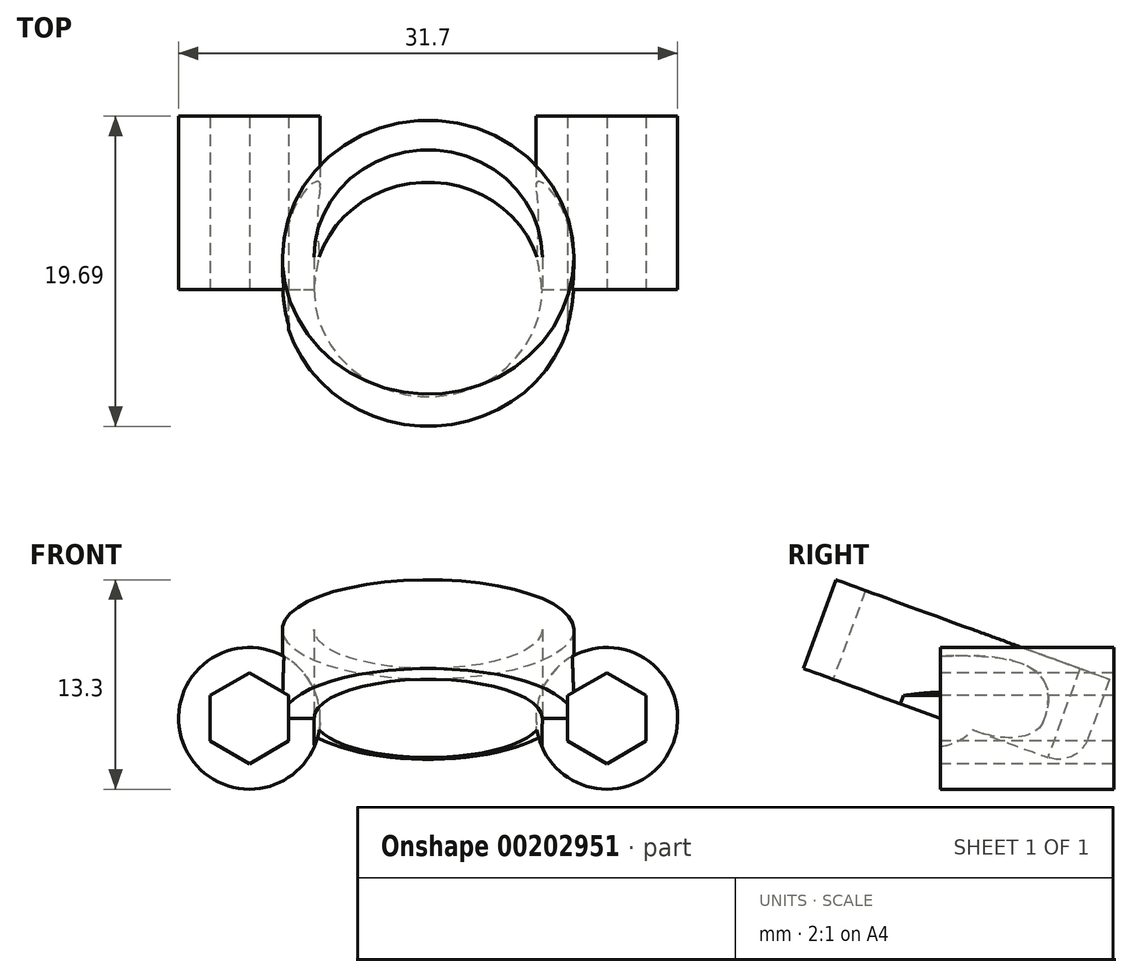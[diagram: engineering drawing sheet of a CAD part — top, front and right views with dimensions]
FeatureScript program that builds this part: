
annotation { "Feature Type Name" : "Feature", "Feature Type Description" : "" }
export const myFeature = defineFeature(function(context is Context, id is Id, definition is map)
    precondition{}
    {
        {
            var Q0;
            Q0=qCreatedBy(makeId("Top.planeOp"),FACE);
            var sketch = newSketch(context, id + "F0", { "sketchPlane" : qUnion([Q0])});
            skCircle(sketch, "E0", {"center": v(0, 0) * mm, "radius": 7.25 * mm});
            skCircle(sketch, "E1", {"center": v(0, 0) * mm, "radius": 9.25 * mm});
            skSolve(sketch);
        }
        {
            var Q0;
            Q0=makeQuery(id+"F0.imprint","IMPRINT",FACE,{"disambiguationData":[TD([[makeQuery(id+"F0.imprint","IMPRINT",EDGE,{"derivedFrom":sQuery(id+"F0.wireOp",EDGE,"E0")}),-1.0]])]});
            extrude(context, id + "F1", {"entities" : qUnion([Q0]), "depth" : 6 * mm});
        }
        {
            var Q0;
            Q0=qCreatedBy(makeId("Top.planeOp"),FACE);
            var sketch = newSketch(context, id + "F2", { "sketchPlane" : qUnion([Q0])});
            skLineSegment(sketch, "E2", {"start": v(-15.14, 0) * mm, "end": v(14.33, 0) * mm});
            skSolve(sketch);
        }
        {
            var Q0;
            Q0=makeQuery(id+"F1.opExtrude","SWEPT_BODY",BODY,{"disambiguationData":[OSD([sQuery(id+"F0.wireOp",EDGE,"E0"),sQuery(id+"F0.wireOp",EDGE,"h9PfKkJo-UdOM-yz0z-Uwii-sodwroVbnJnT.bottom"),sQuery(id+"F0.wireOp",EDGE,"h9PfKkJo-UdOM-yz0z-Uwii-sodwroVbnJnT.top"),sQuery(id+"F0.wireOp",EDGE,"h9PfKkJo-UdOM-yz0z-Uwii-sodwroVbnJnT.left"),sQuery(id+"F0.wireOp",EDGE,"h9PfKkJo-UdOM-yz0z-Uwii-sodwroVbnJnT.right")])]});
            var Q1;
            Q1=sQuery(id+"F2.wireOp",EDGE,"E2");
            var Q2;
            Q2=sQuery(id+"F2.wireOp",EDGE,"E2");
            transform(context, id + "F3", {"entities" : qUnion([Q0]), "transformType" : TransformType.ROTATION, "transformAxis" : qUnion([Q2]), "angle" : 20 * degree, "oppositeDirection" : true, "makeCopy" : false});
        }
        {
            var Q0;
            Q0=qCreatedBy(makeId("Front.planeOp"),FACE);
            var sketch = newSketch(context, id + "F4", { "sketchPlane" : qUnion([Q0])});
            skCircle(sketch, "E3.cCircle", {"center": v(-11.35, 0) * mm, "radius": 2.5 * mm, "construction": true});
            skLineSegment(sketch, "E3.0", {"start": v(-8.85, 1.44) * mm, "end": v(-8.85, -1.44) * mm});
            skLineSegment(sketch, "E3.1", {"start": v(-8.85, -1.44) * mm, "end": v(-11.35, -2.89) * mm});
            skLineSegment(sketch, "E3.2", {"start": v(-11.35, -2.89) * mm, "end": v(-13.85, -1.44) * mm});
            skLineSegment(sketch, "E3.3", {"start": v(-13.85, -1.44) * mm, "end": v(-13.85, 1.44) * mm});
            skLineSegment(sketch, "E3.4", {"start": v(-13.85, 1.44) * mm, "end": v(-11.35, 2.89) * mm});
            skLineSegment(sketch, "E3.5", {"start": v(-11.35, 2.89) * mm, "end": v(-8.85, 1.44) * mm});
            skPoint(sketch, "E3.0.midPoint", {"position": v(-8.85, 0) * mm});
            skCircle(sketch, "E4", {"center": v(-11.35, 0) * mm, "radius": 4.5 * mm});
            skCircle(sketch, "E5.1.0.0", {"center": v(11.35, 0) * mm, "radius": 4.5 * mm});
            skLineSegment(sketch, "E5.1.0.1", {"start": v(11.35, 2.89) * mm, "end": v(13.85, 1.44) * mm});
            skLineSegment(sketch, "E5.1.0.2", {"start": v(8.85, 1.44) * mm, "end": v(11.35, 2.89) * mm});
            skLineSegment(sketch, "E5.1.0.3", {"start": v(8.85, -1.44) * mm, "end": v(8.85, 1.44) * mm});
            skLineSegment(sketch, "E5.1.0.4", {"start": v(11.35, -2.89) * mm, "end": v(8.85, -1.44) * mm});
            skLineSegment(sketch, "E5.1.0.5", {"start": v(13.85, -1.44) * mm, "end": v(11.35, -2.89) * mm});
            skLineSegment(sketch, "E5.1.0.6", {"start": v(13.85, 1.44) * mm, "end": v(13.85, -1.44) * mm});
            skCircle(sketch, "E5.1.0.7", {"center": v(11.35, 0) * mm, "radius": 2.5 * mm, "construction": true});
            skPoint(sketch, "E5.1.0.8", {"position": v(13.85, 0) * mm});
            skLineSegment(sketch, "E5.direction1", {"start": v(-13.85, -1.44) * mm, "end": v(8.85, -1.44) * mm, "construction": true});
            skSolve(sketch);
        }
        {
            var Q0;
            Q0=makeQuery(id+"F4.imprint","IMPRINT",FACE,{"disambiguationData":[TD([[makeQuery(id+"F4.imprint","IMPRINT",EDGE,{"derivedFrom":sQuery(id+"F4.wireOp",EDGE,"E5.1.0.0")}),1.0]])]});
            var Q1;
            Q1=makeQuery(id+"F4.imprint","IMPRINT",FACE,{"disambiguationData":[TD([[makeQuery(id+"F4.imprint","IMPRINT",EDGE,{"derivedFrom":sQuery(id+"F4.wireOp",EDGE,"E3.0")}),1.0]])]});
            var Q2;
            Q2=makeQuery(id+"F1.opExtrude","CAP_VERTEX",VERTEX,{"disambiguationData":[OSD([sQuery(id+"F0.wireOp",EDGE,"h9PfKkJo-UdOM-yz0z-Uwii-sodwroVbnJnT.bottom"),sQuery(id+"F0.wireOp",EDGE,"h9PfKkJo-UdOM-yz0z-Uwii-sodwroVbnJnT.right")])],"isStart":false});
            extrude(context, id + "F5", {"entities" : qUnion([Q0, Q1]), "operationType" : NewBodyOperationType.ADD, "oppositeDirection" : true, "endBoundEntityVertex" : qUnion([Q2]), "depth" : 11 * mm});
        }
        {
            var Q0;
            Q0=makeQuery(id+"F4.imprint","IMPRINT",FACE,{"disambiguationData":[TD([[makeQuery(id+"F4.imprint","IMPRINT",EDGE,{"derivedFrom":sQuery(id+"F4.wireOp",EDGE,"E3.0")}),-1.0]])]});
            var Q1;
            Q1=makeQuery(id+"F4.imprint","IMPRINT",FACE,{"disambiguationData":[TD([[makeQuery(id+"F4.imprint","IMPRINT",EDGE,{"derivedFrom":sQuery(id+"F4.wireOp",EDGE,"E5.1.0.1")}),-1.0]])]});
            extrude(context, id + "F6", {"entities" : qUnion([Q0, Q1]), "operationType" : NewBodyOperationType.REMOVE, "depth" : 50 * mm, "symmetric" : true});
        }
        {
            var Q0;
            {var subQ1=sQuery(id+"F4.wireOp",EDGE,"E3.0");var subQ2=sQuery(id+"F0.wireOp",EDGE,"E1");var subQ3=sQuery(id+"F0.wireOp",EDGE,"E0");Q0=makeQuery(id+"F5.boolean.opBoolean","SPLIT",FACE,{"disambiguationData":[TD([makeQuery(id+"F5.opExtrude","SWEPT_FACE",FACE,{"disambiguationData":[OSD([subQ1])]})])],"derivedFrom":makeQuery(id+"F1.opExtrude","CAP_FACE",FACE,{"disambiguationData":[OSD([subQ3,subQ2])],"isStart":true})});}
            var sketch = newSketch(context, id + "F7", { "sketchPlane" : qUnion([Q0])});
            skCircle(sketch, "E6", {"center": v(0, 0) * mm, "radius": 7.25 * mm});
            skSolve(sketch);
        }
        {
            var Q0;
            Q0=makeQuery(id+"F7.imprint","IMPRINT",FACE,{"disambiguationData":[TD([[makeQuery(id+"F7.imprint","IMPRINT",EDGE,{"derivedFrom":sQuery(id+"F7.wireOp",EDGE,"E6")}),1.0]])]});
            extrude(context, id + "F8", {"entities" : qUnion([Q0]), "operationType" : NewBodyOperationType.REMOVE, "oppositeDirection" : true, "depth" : 50 * mm, "symmetric" : true});
        }
        {
            var Q0;
            {var subQ0=sQuery(id+"F0.wireOp",EDGE,"E1");Q0=makeQuery(id+"F5.boolean.opBoolean","SPLIT",EDGE,{"disambiguationData":[TD([makeQuery(id+"F5.opExtrude","SWEPT_FACE",FACE,{"disambiguationData":[OSD([sQuery(id+"F4.wireOp",EDGE,"E3.1")])]})])],"derivedFrom":makeQuery(id+"F1.opExtrude","CAP_EDGE",EDGE,{"disambiguationData":[OSD([subQ0])],"isStart":true})});}
            var Q1;
            {var subQ0=sQuery(id+"F0.wireOp",EDGE,"E1");Q1=makeQuery(id+"F5.boolean.opBoolean","SPLIT",EDGE,{"disambiguationData":[TD([makeQuery(id+"F5.opExtrude","SWEPT_FACE",FACE,{"disambiguationData":[OSD([sQuery(id+"F4.wireOp",EDGE,"E4")])]})])],"derivedFrom":makeQuery(id+"F1.opExtrude","CAP_EDGE",EDGE,{"disambiguationData":[OSD([subQ0])],"isStart":true})});}
            fillet(context, id + "F9", {"entities" : qUnion([Q0, Q1]), "radius" : 2 * mm, "tangentPropagation" : true, "allowEdgeOverflow" : false});
        }
    });
